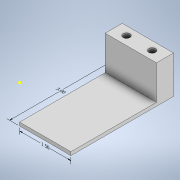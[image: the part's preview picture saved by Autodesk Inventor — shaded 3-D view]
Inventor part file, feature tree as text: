
AUTODESK INVENTOR PART (.ipt)
format: ipt  version: 2020 (Build 240168000, 168)  size: 122,880 bytes
history: native  units: in
note: dims shown in document units (in); Inventor stores cm internally (conversion verified against a paired STEP export)
features: sketch x4, other x3, extrude x2, hole x1
ambient origin geometry x8: Origin, YZ Plane, XZ Plane, XY Plane, X Axis, Y Axis, Z Axis, Center Point
bodies: Solid1 (feature_tree)
feature tree (10):
  other  "Annotations"
  extrude  "Extrusion1"  Depth=3.0in
  extrude  "Extrusion2"  Depth=1.5in
  sketch  "Sketch5"  dims[d5=0.5in d6=1.0in d7=0.0in]
  hole  "Hole1"  [1 undecoded]
  sketch  "Sketch1"  dims[d0=1.5in d1=3.0in]
  sketch  "Sketch2"  dims[d2=0.1in d3=0.0in d4=1.5in]
  sketch  "Sketch6"  dims[d8=0.375in d9=0.375in d10=0.2in d11=0.75in d12=0.75in d13=0.188in d14=0.5635in d15=0.5in d16=0.8108in d17=0.0in d18=0.3937in d19=1.5in d20=0.1641in d21=0.2363in d22=3.0in]
  other  "Linear Dimension 1"
  other  "Linear Dimension 2"
note: 1 required parameter value undecoded (feature->parameter linkage not recoverable at this tier; creation-order binding heuristic only, values carry confidence <= 0.55)
